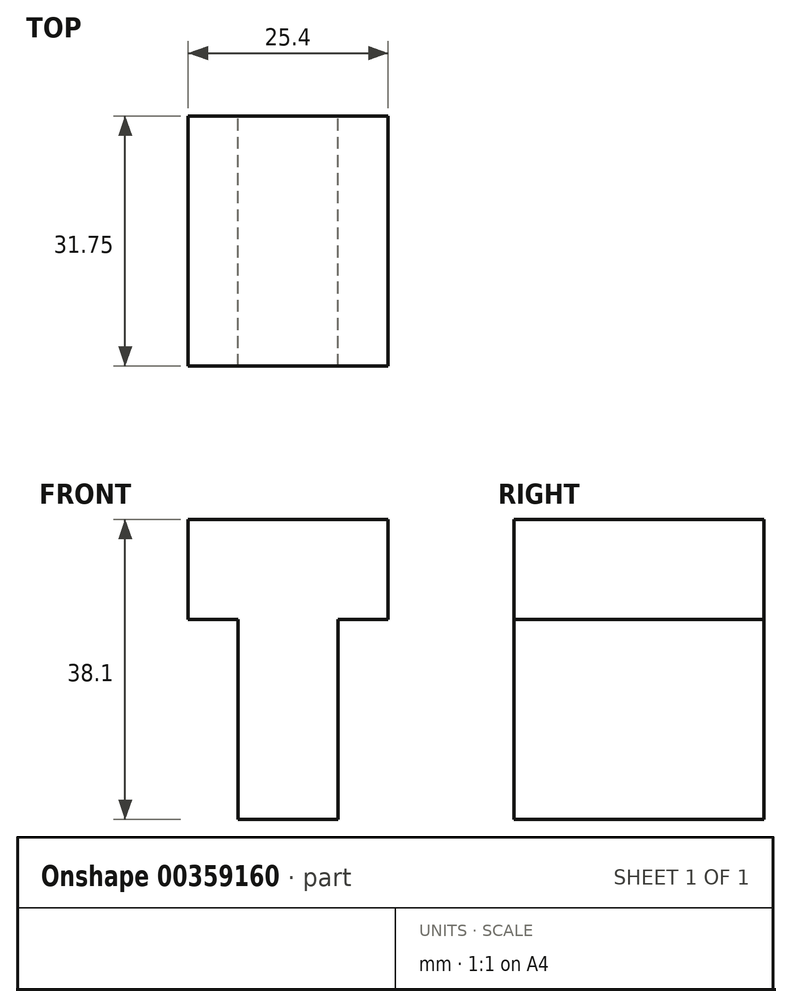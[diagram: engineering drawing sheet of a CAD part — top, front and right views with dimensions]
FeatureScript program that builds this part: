
annotation { "Feature Type Name" : "Feature", "Feature Type Description" : "" }
export const myFeature = defineFeature(function(context is Context, id is Id, definition is map)
    precondition{}
    {
        {
            var Q0;
            Q0=qCreatedBy(makeId("Front.planeOp"),FACE);
            var sketch = newSketch(context, id + "F0", { "sketchPlane" : qUnion([Q0])});
            skLineSegment(sketch, "E0", {"start": v(-12.85, 12.7) * mm, "end": v(12.55, 12.7) * mm});
            skLineSegment(sketch, "E1", {"start": v(12.55, 12.7) * mm, "end": v(12.55, 0) * mm});
            skLineSegment(sketch, "E2", {"start": v(12.55, 0) * mm, "end": v(6.2, 0) * mm});
            skLineSegment(sketch, "E3", {"start": v(6.2, 0) * mm, "end": v(6.2, -25.4) * mm});
            skLineSegment(sketch, "E4", {"start": v(6.2, -25.4) * mm, "end": v(-6.5, -25.4) * mm});
            skLineSegment(sketch, "E5", {"start": v(-6.5, -25.4) * mm, "end": v(-6.5, 0) * mm});
            skLineSegment(sketch, "E6", {"start": v(-6.5, 0) * mm, "end": v(-12.85, 0) * mm});
            skLineSegment(sketch, "E7", {"start": v(-12.85, 0) * mm, "end": v(-12.85, 12.7) * mm});
            skSolve(sketch);
        }
        {
            var Q0;
            Q0 = qSketchRegion(id + "F0", true);
            extrude(context, id + "F1", {"entities" : qUnion([Q0]), "depth" : 31.75 * mm});
        }
    });
